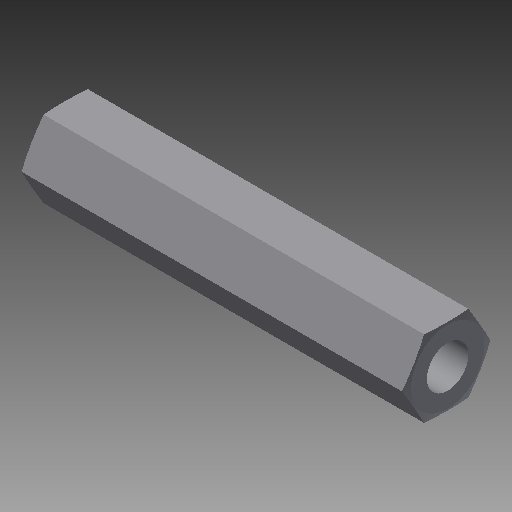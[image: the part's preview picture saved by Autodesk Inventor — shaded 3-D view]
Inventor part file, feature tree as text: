
AUTODESK INVENTOR PART (.ipt)
format: ipt  version: 2018 (Build 220112000, 112)  size: 95,744 bytes
history: native  units: in
note: dims shown in document units (in); Inventor stores cm internally (conversion verified against a paired STEP export)
features: mirror x1, other x1, imported_body x1
ambient origin geometry x8: Origin, YZ Plane, XZ Plane, XY Plane, X Axis, Y Axis, Z Axis, Center Point
bodies: Body1 (feature_tree)
feature tree (3):
  mirror  "Mirror1"
  other  "217-2588-006 Rev1.ipt1"
  imported_body  "Base1"
